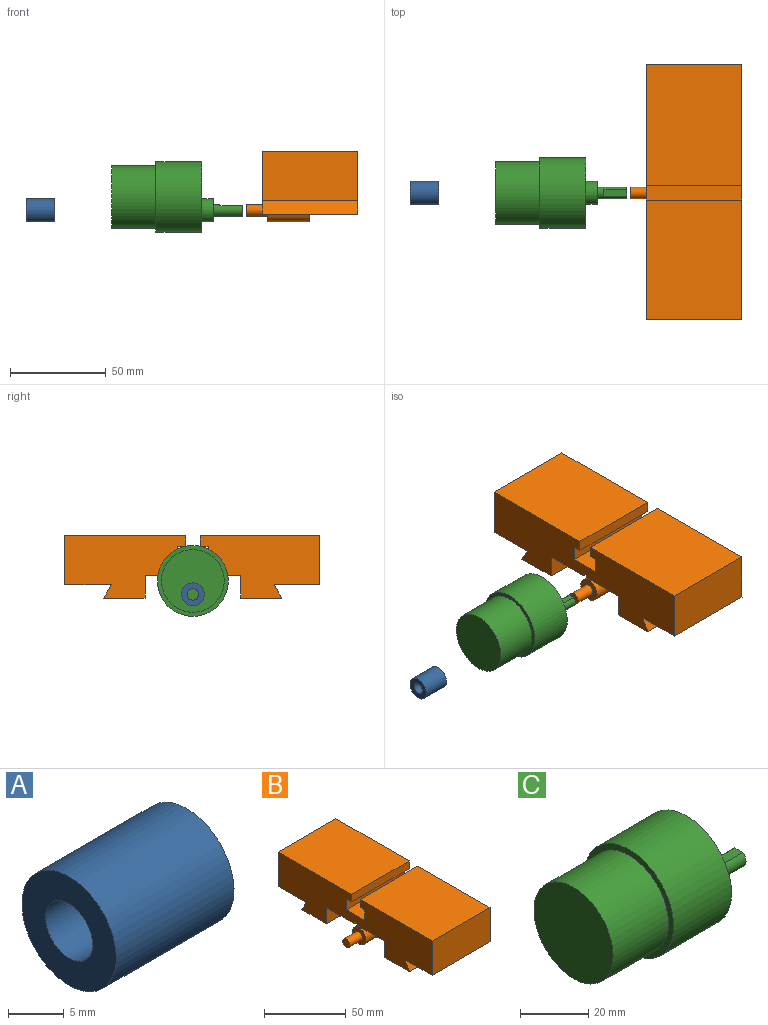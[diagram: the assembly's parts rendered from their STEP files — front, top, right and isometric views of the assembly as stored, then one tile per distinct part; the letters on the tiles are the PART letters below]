
ASSEMBLY  parts=3 mates=2
PART A: 4 faces, bbox 15x12x12 mm
  f0: cylinder r=3mm len=15mm, axis (-1,0,0), area 282.7mm2, adj f2,f3
  f1: cylinder r=6mm len=15mm, axis (-1,0,0), area 565.5mm2, adj f2,f3
  f2: plane 12x12mm, normal (1,0,0), area 84.8mm2, adj f0,f1
  f3: plane 12x12mm, normal (-1,0,0), area 84.8mm2, adj f0,f1
PART B: 38 faces, bbox 58x133.1x36.6 mm
  f0: plane 3x1.41mm, normal (0,1,0), area 4.2mm2, adj f1,f16,f28,f34
  f1: plane 3x2.03mm, normal (0,0,-1), area 6.1mm2, adj f0,f2,f28,f34
  f2: plane 3x1.41mm, normal (0,-1,0), area 4.2mm2, adj f1,f20,f28,f34
  f3: plane 50x5.71mm, normal (0,-1,0), area 285.5mm2, adj f4,f26,f27,f28
  f4: plane 50x4.32mm, normal (0,0,-1), area 216.2mm2, adj f3,f5,f27,f28
  f5: plane 50x7.93mm, normal (0,-1,0), area 396.5mm2, adj f4,f6,f27,f28
  f6: plane 50x16mm, normal (0,0,1), area 800mm2, adj f5,f7,f27,f28
  f7: plane 50x7.93mm, normal (0,1,0), area 396.5mm2, adj f6,f8,f27,f28
  f8: plane 50x4.14mm, normal (0,0,-1), area 207.2mm2, adj f7,f9,f27,f28
  f9: plane 50x5.71mm, normal (0,1,0), area 285.5mm2, adj f8,f10,f27,f28
  f10: plane 62.23x50mm, normal (0,0,1), area 3111.6mm2, adj f9,f11,f27,f28
  f11: plane 50x25.64mm, normal (0,-1,0), area 1282.1mm2, adj f10,f12,f27,f28
  f12: plane 50x23.59mm, normal (0,0,-1), area 1179.5mm2, adj f11,f13,f27,f28
  f13: plane 50x7mm, normal (0,-0.87,0.5), area 404.1mm2, adj f12,f14,f27,f28
  f14: plane 50x21.54mm, normal (0,0,-1), area 1077.1mm2, adj f13,f15,f27,f28
  f15: plane 50x12mm, normal (0,1,0), area 600mm2, adj f14,f16,f27,f28
  f16: plane 50x24.04mm, normal (0,0,-1), area 1202mm2, adj f0,f15,f17,f27,f28,f29
  f17: plane 25x1.41mm, normal (0,1,0), area 35.2mm2, adj f16,f18,f27,f33
  f18: plane 25x2.03mm, normal (0,0,-1), area 50.9mm2, adj f17,f19,f27,f33
  f19: plane 25x1.41mm, normal (0,-1,0), area 35.2mm2, adj f18,f20,f27,f33
  f20: plane 50x23.93mm, normal (0,0,-1), area 1196.3mm2, adj f2,f19,f21,f27,f28,f30
  f21: plane 50x12mm, normal (0,-1,0), area 600mm2, adj f20,f22,f27,f28
  f22: plane 50x21.54mm, normal (0,0,-1), area 1077.1mm2, adj f21,f23,f27,f28
  f23: plane 50x7mm, normal (0,0.87,0.5), area 404.1mm2, adj f22,f24,f27,f28
  f24: plane 50x24.49mm, normal (0,0,-1), area 1224.4mm2, adj f23,f25,f27,f28
  f25: plane 50x25.64mm, normal (0,1,0), area 1282.1mm2, adj f24,f26,f27,f28
  f26: plane 63.31x50mm, normal (0,0,1), area 3165.6mm2, adj f3,f25,f27,f28
  f27: plane 133.08x32.64mm, normal (1,0,0), area 3262.8mm2, adj f3,f4,f5,f6,f7,f8,f9,f10
  f28: plane 133.08x32.64mm, normal (-1,0,0), area 3262.8mm2, adj f0,f1,f2,f3,f4,f5,f6,f7
  f29: plane 22x4.08mm, normal (0,-1,0), area 89.7mm2, adj f16,f31,f33,f34
  f30: plane 22x4.1mm, normal (0,1,0), area 90.1mm2, adj f20,f31,f33,f34
  f31: cylinder r=6mm len=22mm, axis (-1,0,0), area 784.4mm2, adj f29,f30,f33,f34
  f32: cylinder r=1.25mm len=22mm, axis (-1,0,0), area 172.8mm2, adj f33,f37
  f33: plane 17.41x12mm, normal (1,0,0), area 119.2mm2, adj f17,f18,f19,f29,f30,f31,f32
  f34: plane 17.41x12mm, normal (-1,0,0), area 95.9mm2, adj f0,f1,f2,f29,f30,f31,f36
  f35: plane 6x6mm, normal (-1,0,0), area 28.3mm2, adj f36
  f36: cylinder r=3mm len=11mm, axis (1,0,0), area 207.3mm2, adj f34,f35
  f37: plane 2.5x2.5mm, normal (1,0,0), area 4.9mm2, adj f32
PART C: 23 faces, bbox 68.5x37x37 mm
  f0: cylinder r=18.5mm len=37mm, axis (-1,0,0), area 2789.7mm2, adj f1,f2
  f1: plane 37x37mm, normal (1,0,0), area 919.7mm2, adj f0,f5,f9,f11,f13,f15,f17,f19
  f2: plane 37x37mm, normal (-1,0,0), area 230.2mm2, adj f0,f3
  f3: cylinder r=16.4mm len=32.8mm, axis (1,0,0), area 2370mm2, adj f2,f4
  f4: plane 32.8x32.8mm, normal (-1,0,0), area 845mm2, adj f3
  f5: cylinder r=6mm len=12mm, axis (-1,0,0), area 226.2mm2, adj f1,f6
  f6: plane 12x12mm, normal (1,0,0), area 84.8mm2, adj f5,f7
  f7: cylinder r=3mm len=15.5mm, axis (-1,0,0), area 250mm2, adj f6,f8,f21,f22
  f8: plane 6x5.5mm, normal (1,0,0), area 27.1mm2, adj f7,f21
  f9: cylinder r=1.5mm len=5mm, axis (1,0,0), area 47.1mm2, adj f1,f10
  f10: plane 3x3mm, normal (1,0,0), area 7.1mm2, adj f9
  f11: cylinder r=1.5mm len=5mm, axis (1,0,0), area 47.1mm2, adj f1,f12
  f12: plane 3x3mm, normal (1,0,0), area 7.1mm2, adj f11
  f13: cylinder r=1.5mm len=5mm, axis (1,0,0), area 47.1mm2, adj f1,f14
  f14: plane 3x3mm, normal (1,0,0), area 7.1mm2, adj f13
  f15: cylinder r=1.5mm len=5mm, axis (1,0,0), area 47.1mm2, adj f1,f16
  f16: plane 3x3mm, normal (1,0,0), area 7.1mm2, adj f15
  f17: cylinder r=1.5mm len=5mm, axis (1,0,0), area 47.1mm2, adj f1,f18
  f18: plane 3x3mm, normal (1,0,0), area 7.1mm2, adj f17
  f19: cylinder r=1.5mm len=5mm, axis (1,0,0), area 47.1mm2, adj f1,f20
  f20: plane 3x3mm, normal (1,0,0), area 7.1mm2, adj f19
  f21: plane 12x3.32mm, normal (0,0,1), area 39.8mm2, adj f7,f8,f22
  f22: plane 3.32x0.5mm, normal (1,0,0), area 1.1mm2, adj f7,f21
PLACE A t=(-69.67,-14.84,-3.45)mm
PLACE B rot(axis=(-0.99,0.06,0.15),0deg) t=(53.53,-14.84,-3.45)mm
PLACE C t=(-1.97,-14.84,3.55)mm
MATE cylindrical C.f5 <-> A.f0  axis (1,0,0) through (43.53,-14.84,-3.45)mm
MATE slider C.f5 <-> B.f31  axis (1,0,0) through (43.53,-14.84,-3.45)mm
